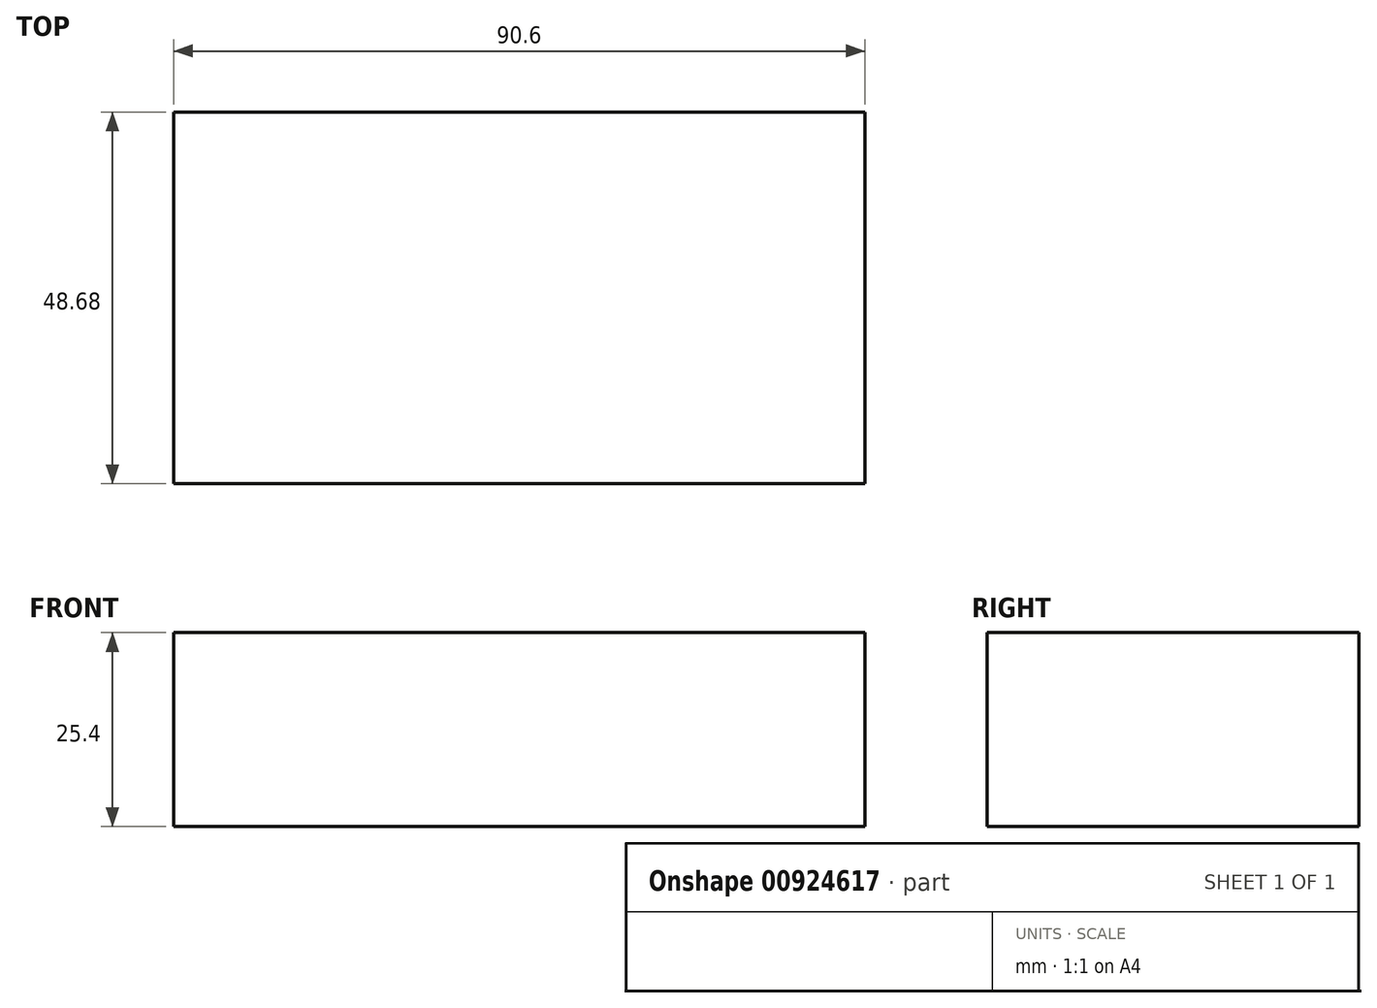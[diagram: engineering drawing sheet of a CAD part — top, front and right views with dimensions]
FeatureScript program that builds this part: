
annotation { "Feature Type Name" : "Feature", "Feature Type Description" : "" }
export const myFeature = defineFeature(function(context is Context, id is Id, definition is map)
    precondition{}
    {
        {
            var Q0;
            Q0=qCreatedBy(makeId("Top.planeOp"),FACE);
            var sketch = newSketch(context, id + "F0", { "sketchPlane" : qUnion([Q0])});
            skLineSegment(sketch, "E0.bottom", {"start": v(45.3, 24.34) * mm, "end": v(-45.3, 24.34) * mm});
            skLineSegment(sketch, "E0.top", {"start": v(45.3, -24.34) * mm, "end": v(-45.3, -24.34) * mm});
            skLineSegment(sketch, "E0.left", {"start": v(45.3, 24.34) * mm, "end": v(45.3, -24.34) * mm});
            skLineSegment(sketch, "E0.right", {"start": v(-45.3, 24.34) * mm, "end": v(-45.3, -24.34) * mm});
            skPoint(sketch, "E0.middle", {"position": v(0, 0) * mm});
            skSolve(sketch);
        }
        {
            var Q0;
            Q0=makeQuery(id+"F0.imprint","IMPRINT",FACE,{"disambiguationData":[TD([[makeQuery(id+"F0.imprint","IMPRINT",EDGE,{"derivedFrom":sQuery(id+"F0.wireOp",EDGE,"E0.bottom")}),1.0]])]});
            extrude(context, id + "F1", {"entities" : qUnion([Q0]), "depth" : 25.4 * mm, "offsetDistance" : 25.4 * mm});
        }
    });
